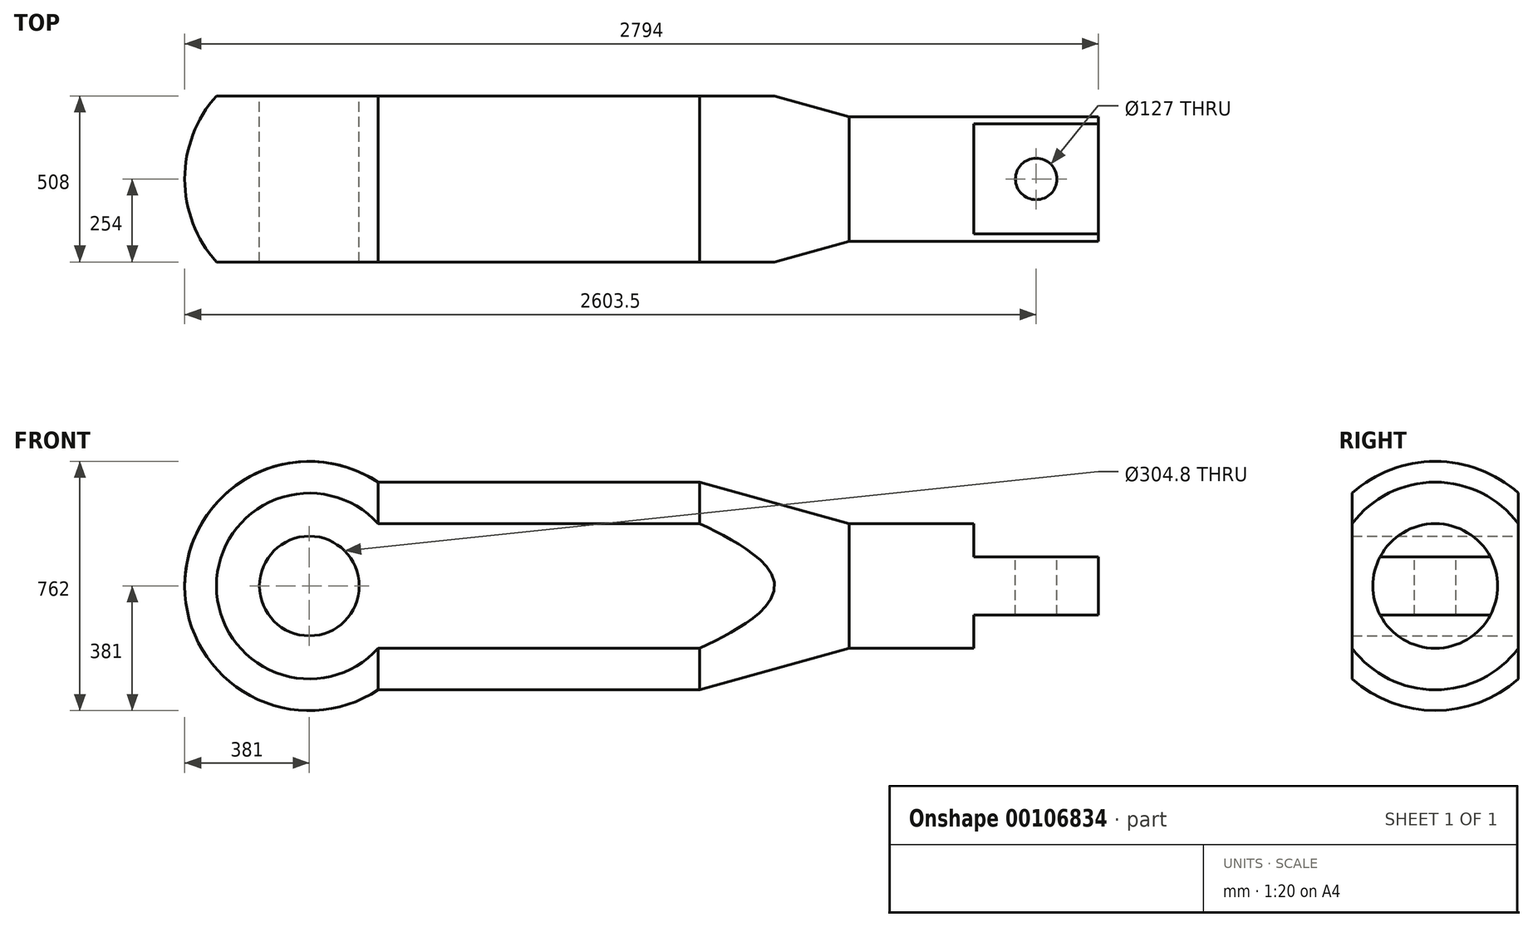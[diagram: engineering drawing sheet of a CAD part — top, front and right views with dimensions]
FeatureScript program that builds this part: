
annotation { "Feature Type Name" : "Feature", "Feature Type Description" : "" }
export const myFeature = defineFeature(function(context is Context, id is Id, definition is map)
    precondition{}
    {
        {
            var Q0;
            Q0=qCreatedBy(makeId("Front.planeOp"),FACE);
            var sketch = newSketch(context, id + "F0", { "sketchPlane" : qUnion([Q0])});
            skLineSegment(sketch, "E0", {"start": v(0, 0) * mm, "end": v(2032, 0) * mm});
            skLineSegment(sketch, "E1", {"start": v(210.6, 317.5) * mm, "end": v(1193.8, 317.5) * mm});
            skLineSegment(sketch, "E2", {"start": v(1193.8, 317.5) * mm, "end": v(1651, 190.5) * mm});
            skLineSegment(sketch, "E3", {"start": v(1651, 190.5) * mm, "end": v(2032, 190.5) * mm});
            skLineSegment(sketch, "E4", {"start": v(2032, 190.5) * mm, "end": v(2032, 0) * mm});
            skArc(sketch, "E5", {"start": v(-381, 0) * mm, "mid": v(-180.17, 335.7) * mm, "end": v(210.6, 317.5) * mm});
            skLineSegment(sketch, "E6", {"start": v(0, 0) * mm, "end": v(-381, 0) * mm});
            skCircle(sketch, "E7", {"center": v(0, 0) * mm, "radius": 152.4 * mm});
            skSolve(sketch);
        }
        {
            var Q0;
            Q0=makeQuery(id+"F0.imprint","IMPRINT",FACE,{"disambiguationData":[TD([[makeQuery(id+"F0.imprint","IMPRINT",EDGE,{"derivedFrom":sQuery(id+"F0.wireOp",EDGE,"E1")}),-1.0]])]});
            var Q1;
            {var subQ3=sQuery(id+"F0.wireOp",EDGE,"RuKDeoje-Rna6-uAsP-8DCh-blyayRj6NzIm");Q1=makeQuery(id+"F0.imprint","IMPRINT",FACE,{"disambiguationData":[TD([[makeQuery(id+"F0.imprint","IMPRINT",EDGE,{"derivedFrom":subQ3}),-1.0]])]});}
            var Q2;
            Q2=sQuery(id+"F0.wireOp",EDGE,"E6");
            revolve(context, id + "F1", {"entities" : qUnion([Q0, Q1]), "axis" : qUnion([Q2]), "revolveType" : RevolveType.FULL});
        }
        {
            var Q0;
            Q0=makeQuery(id+"F1.opRevolve","SWEPT_FACE",FACE,{"disambiguationData":[OSD([sQuery(id+"F0.wireOp",EDGE,"E4")])]});
            var sketch = newSketch(context, id + "F2", { "sketchPlane" : qUnion([Q0])});
            skLineSegment(sketch, "E8", {"start": v(-168.48, 88.9) * mm, "end": v(168.48, 88.9) * mm});
            skLineSegment(sketch, "E9", {"start": v(168.48, -88.9) * mm, "end": v(-168.48, -88.9) * mm});
            skSolve(sketch);
        }
        {
            var Q0;
            {var subQ0=sQuery(id+"F2.wireOp",EDGE,"E8");Q0=makeQuery(id+"F2.imprint","IMPRINT",FACE,{"disambiguationData":[TD([[makeQuery(id+"F2.imprint","IMPRINT",EDGE,{"derivedFrom":subQ0}),-1.0]])]});}
            extrude(context, id + "F3", {"entities" : qUnion([Q0]), "operationType" : NewBodyOperationType.ADD, "depth" : 381 * mm});
        }
        {
            var Q0;
            Q0=makeQuery(id+"F3.opExtrude","SWEPT_FACE",FACE,{"disambiguationData":[OSD([sQuery(id+"F2.wireOp",EDGE,"E8")])]});
            var sketch = newSketch(context, id + "F4", { "sketchPlane" : qUnion([Q0])});
            skLineSegment(sketch, "E10", {"start": v(2032, -168.48) * mm, "end": v(2413, 168.48) * mm, "construction": true});
            skCircle(sketch, "E11", {"center": v(2222.5, 0) * mm, "radius": 63.5 * mm});
            skSolve(sketch);
        }
        {
            var Q0;
            Q0 = qSketchRegion(id + "F4", true);
            extrude(context, id + "F5", {"entities" : qUnion([Q0]), "operationType" : NewBodyOperationType.REMOVE, "endBound" : BoundingType.THROUGH_ALL, "oppositeDirection" : true, "depth" : 25.4 * mm});
        }
        {
            var Q0;
            Q0=makeQuery(id+"F3.opExtrude","CAP_FACE",FACE,{"disambiguationData":[OSD([sQuery(id+"F0.wireOp",EDGE,"E3"),sQuery(id+"F0.wireOp",EDGE,"E4"),sQuery(id+"F2.wireOp",EDGE,"E8"),sQuery(id+"F2.wireOp",EDGE,"E9")])],"isStart":false});
            var sketch = newSketch(context, id + "F6", { "sketchPlane" : qUnion([Q0])});
            skLineSegment(sketch, "E12", {"start": v(0, 0) * mm, "end": v(254, 0) * mm, "construction": true});
            skPoint(sketch, "E12.endSnap0", {"position": v(190.5, 0) * mm});
            skLineSegment(sketch, "E13", {"start": v(0, 0) * mm, "end": v(-254, 0) * mm, "construction": true});
            skPoint(sketch, "E13.endSnap0", {"position": v(-190.5, 0) * mm});
            skLineSegment(sketch, "E14", {"start": v(-254, 0) * mm, "end": v(-254, 437.95) * mm});
            skLineSegment(sketch, "E15", {"start": v(-254, 437.95) * mm, "end": v(-254, -433.27) * mm});
            skLineSegment(sketch, "E16", {"start": v(254, -433.27) * mm, "end": v(254, 437.95) * mm});
            skLineSegment(sketch, "E17", {"start": v(254, 437.95) * mm, "end": v(393.7, 437.95) * mm});
            skLineSegment(sketch, "E18", {"start": v(393.7, 437.95) * mm, "end": v(393.7, -433.27) * mm});
            skLineSegment(sketch, "E19", {"start": v(393.7, -433.27) * mm, "end": v(254, -433.27) * mm});
            skLineSegment(sketch, "E20", {"start": v(-254, -433.27) * mm, "end": v(-393.7, -433.27) * mm});
            skLineSegment(sketch, "E21", {"start": v(-393.7, -433.27) * mm, "end": v(-393.7, 437.95) * mm});
            skLineSegment(sketch, "E22", {"start": v(-393.7, 437.95) * mm, "end": v(-254, 437.95) * mm});
            skSolve(sketch);
        }
        {
            var Q0;
            Q0=makeQuery(id+"F6.imprint","IMPRINT",FACE,{"disambiguationData":[TD([[makeQuery(id+"F6.imprint","IMPRINT",EDGE,{"derivedFrom":sQuery(id+"F6.wireOp",EDGE,"E16")}),-1.0]])]});
            var Q1;
            {var subQ2=sQuery(id+"F6.wireOp",EDGE,"E20");Q1=makeQuery(id+"F6.imprint","IMPRINT",FACE,{"disambiguationData":[TD([[makeQuery(id+"F6.imprint","IMPRINT",EDGE,{"derivedFrom":subQ2}),-1.0]])]});}
            extrude(context, id + "F7", {"entities" : qUnion([Q0, Q1]), "operationType" : NewBodyOperationType.REMOVE, "endBound" : BoundingType.THROUGH_ALL, "oppositeDirection" : true, "depth" : 25.4 * mm});
        }
        {
            var Q0;
            {var subQ0=sQuery(id+"F0.wireOp",EDGE,"E6");var subQ1=sQuery(id+"F0.wireOp",EDGE,"E0");var subQ2=makeQuery(id+"F0.imprint","INTERSECT",VERTEX,{"derivedFrom":[subQ1,subQ0]});Q0=makeQuery(id+"F0.imprint","IMPRINT",FACE,{"disambiguationData":[TD([[makeQuery(id+"F0.imprint","IMPRINT",EDGE,{"disambiguationData":[TD([[subQ2,-1.0]])],"derivedFrom":subQ1}),1.0]])]});}
            var Q1;
            {var subQ0=sQuery(id+"F0.wireOp",EDGE,"E6");var subQ1=sQuery(id+"F0.wireOp",EDGE,"E0");var subQ2=makeQuery(id+"F0.imprint","INTERSECT",VERTEX,{"derivedFrom":[subQ1,subQ0]});Q1=makeQuery(id+"F0.imprint","IMPRINT",FACE,{"disambiguationData":[TD([[makeQuery(id+"F0.imprint","IMPRINT",EDGE,{"disambiguationData":[TD([[subQ2,-1.0]])],"derivedFrom":subQ1}),-1.0]])]});}
            extrude(context, id + "F8", {"entities" : qUnion([Q0, Q1]), "operationType" : NewBodyOperationType.REMOVE, "endBound" : BoundingType.THROUGH_ALL, "depth" : 25.4 * mm, "hasSecondDirection" : true, "secondDirectionBound" : SecondDirectionBoundingType.THROUGH_ALL, "secondDirectionOppositeDirection" : true, "secondDirectionDepth" : 25.4 * mm});
        }
    });
